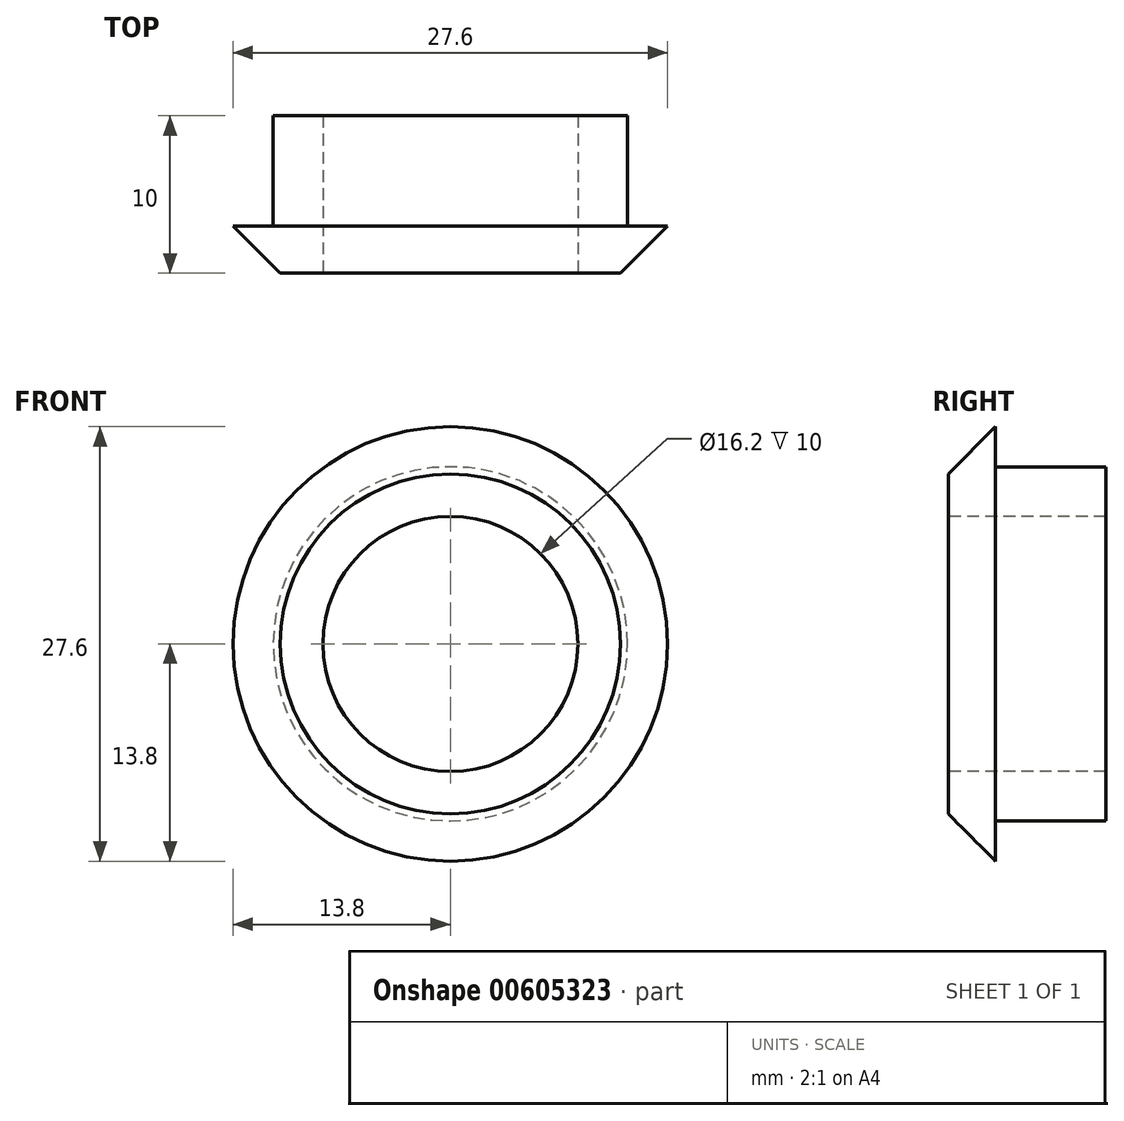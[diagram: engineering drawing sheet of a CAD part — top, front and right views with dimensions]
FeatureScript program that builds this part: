
annotation { "Feature Type Name" : "Feature", "Feature Type Description" : "" }
export const myFeature = defineFeature(function(context is Context, id is Id, definition is map)
    precondition{}
    {
        {
            var Q0;
            Q0=qCreatedBy(makeId("Front.planeOp"),FACE);
            var sketch = newSketch(context, id + "F0", { "sketchPlane" : qUnion([Q0])});
            skCircle(sketch, "E0", {"center": v(0, 0) * mm, "radius": 13.8 * mm});
            skSolve(sketch);
        }
        {
            var Q0;
            Q0 = qSketchRegion(id + "F0", true);
            extrude(context, id + "F1", {"entities" : qUnion([Q0]), "depth" : 3 * mm, "offsetDistance" : 25 * mm});
        }
        {
            var Q0;
            Q0=makeQuery(id+"F1.opExtrude","CAP_FACE",FACE,{"disambiguationData":[OSD([sQuery(id+"F0.wireOp",EDGE,"E0")])],"isStart":false});
            var sketch = newSketch(context, id + "F2", { "sketchPlane" : qUnion([Q0])});
            skCircle(sketch, "E1", {"center": v(0, 0) * mm, "radius": 11.25 * mm});
            skCircle(sketch, "E2", {"center": v(0, 0) * mm, "radius": 8.1 * mm});
            skSolve(sketch);
        }
        {
            var Q0;
            Q0=makeQuery(id+"F2.imprint","IMPRINT",FACE,{"disambiguationData":[TD([[makeQuery(id+"F2.imprint","IMPRINT",EDGE,{"derivedFrom":sQuery(id+"F2.wireOp",EDGE,"E2")}),1.0]])]});
            extrude(context, id + "F3", {"entities" : qUnion([Q0]), "operationType" : NewBodyOperationType.REMOVE, "oppositeDirection" : true, "depth" : 25 * mm, "offsetDistance" : 25 * mm});
        }
        {
            var Q0;
            Q0=makeQuery(id+"F2.imprint","IMPRINT",FACE,{"disambiguationData":[TD([[makeQuery(id+"F2.imprint","IMPRINT",EDGE,{"derivedFrom":sQuery(id+"F2.wireOp",EDGE,"E1")}),1.0]])]});
            extrude(context, id + "F4", {"entities" : qUnion([Q0]), "operationType" : NewBodyOperationType.ADD, "oppositeDirection" : true, "depth" : 10 * mm, "offsetDistance" : 25 * mm});
        }
        {
            var Q0;
            Q0=makeQuery(id+"F1.opExtrude","CAP_EDGE",EDGE,{"disambiguationData":[OSD([sQuery(id+"F0.wireOp",EDGE,"E0")])],"isStart":false});
            chamfer(context, id + "F5", {"entities" : qUnion([Q0]), "width" : 3 * mm, "tangentPropagation" : true});
        }
    });
